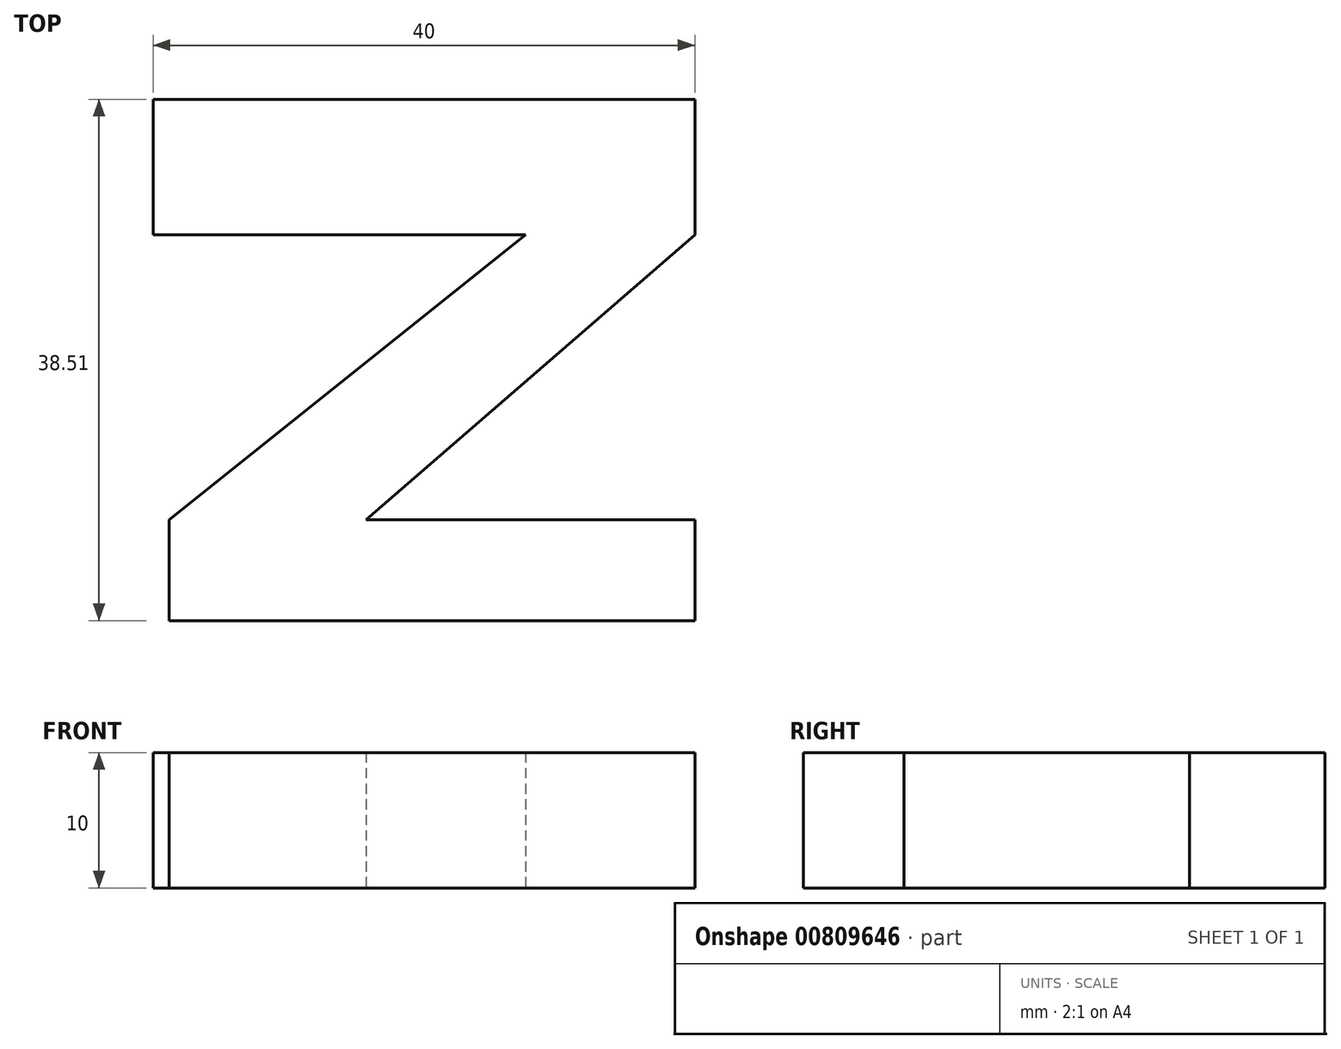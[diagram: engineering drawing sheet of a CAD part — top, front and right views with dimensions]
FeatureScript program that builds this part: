
annotation { "Feature Type Name" : "Feature", "Feature Type Description" : "" }
export const myFeature = defineFeature(function(context is Context, id is Id, definition is map)
    precondition{}
    {
        {
            var Q0;
            Q0=qCreatedBy(makeId("Top.planeOp"),FACE);
            var sketch = newSketch(context, id + "F0", { "sketchPlane" : qUnion([Q0])});
            skLineSegment(sketch, "E0.bottom", {"start": v(0, 0) * mm, "end": v(-40, 0) * mm});
            skLineSegment(sketch, "E0.top", {"start": v(0, 10) * mm, "end": v(-40, 10) * mm});
            skLineSegment(sketch, "E0.left", {"start": v(0, 0) * mm, "end": v(0, 10) * mm});
            skLineSegment(sketch, "E0.right", {"start": v(-40, 0) * mm, "end": v(-40, 10) * mm});
            skLineSegment(sketch, "E1", {"start": v(0, 10) * mm, "end": v(-38.83, -21.06) * mm});
            skLineSegment(sketch, "E2", {"start": v(-38.83, -21.06) * mm, "end": v(-32.87, -28.51) * mm});
            skLineSegment(sketch, "E3", {"start": v(-32.87, -28.51) * mm, "end": v(0, 0) * mm});
            skLineSegment(sketch, "E4.bottom", {"start": v(-38.83, -21.06) * mm, "end": v(0, -21.06) * mm});
            skLineSegment(sketch, "E4.top", {"start": v(-38.83, -28.51) * mm, "end": v(0, -28.51) * mm});
            skLineSegment(sketch, "E4.left", {"start": v(-38.83, -21.06) * mm, "end": v(-38.83, -28.51) * mm});
            skLineSegment(sketch, "E4.right", {"start": v(0, -21.06) * mm, "end": v(0, -28.51) * mm});
            skSolve(sketch);
        }
        {
            var Q0;
            {var subQ4=sQuery(id+"F0.wireOp",EDGE,"E0.top");Q0=makeQuery(id+"F0.imprint","IMPRINT",FACE,{"disambiguationData":[TD([[makeQuery(id+"F0.imprint","IMPRINT",EDGE,{"derivedFrom":subQ4}),1.0]])]});}
            var Q1;
            {var subQ0=sQuery(id+"F0.wireOp",EDGE,"E2");Q1=makeQuery(id+"F0.imprint","IMPRINT",FACE,{"disambiguationData":[TD([[makeQuery(id+"F0.imprint","IMPRINT",EDGE,{"derivedFrom":subQ0}),-1.0]])]});}
            var Q2;
            {var subQ5=sQuery(id+"F0.wireOp",EDGE,"E4.right");Q2=makeQuery(id+"F0.imprint","IMPRINT",FACE,{"disambiguationData":[TD([[makeQuery(id+"F0.imprint","IMPRINT",EDGE,{"derivedFrom":subQ5}),-1.0]])]});}
            var Q3;
            {var subQ0=sQuery(id+"F0.wireOp",EDGE,"E0.left");Q3=makeQuery(id+"F0.imprint","IMPRINT",FACE,{"disambiguationData":[TD([[makeQuery(id+"F0.imprint","IMPRINT",EDGE,{"derivedFrom":subQ0}),1.0]])]});}
            var Q4;
            {var subQ1=sQuery(id+"F0.wireOp",EDGE,"E0.bottom");var subQ3=sQuery(id+"F0.wireOp",EDGE,"E1");var subQ4=makeQuery(id+"F0.imprint","INTERSECT",VERTEX,{"derivedFrom":[subQ1,subQ3]});Q4=makeQuery(id+"F0.imprint","IMPRINT",FACE,{"disambiguationData":[TD([[makeQuery(id+"F0.imprint","IMPRINT",EDGE,{"disambiguationData":[TD([[subQ4,1.0]])],"derivedFrom":subQ1}),1.0]])]});}
            var Q5;
            {var subQ0=sQuery(id+"F0.wireOp",EDGE,"E2");Q5=makeQuery(id+"F0.imprint","IMPRINT",FACE,{"disambiguationData":[TD([[makeQuery(id+"F0.imprint","IMPRINT",EDGE,{"derivedFrom":subQ0}),1.0]])]});}
            extrude(context, id + "F1", {"entities" : qUnion([Q0, Q1, Q2, Q3, Q4, Q5]), "depth" : 10 * mm, "offsetDistance" : 25.4 * mm});
        }
    });
